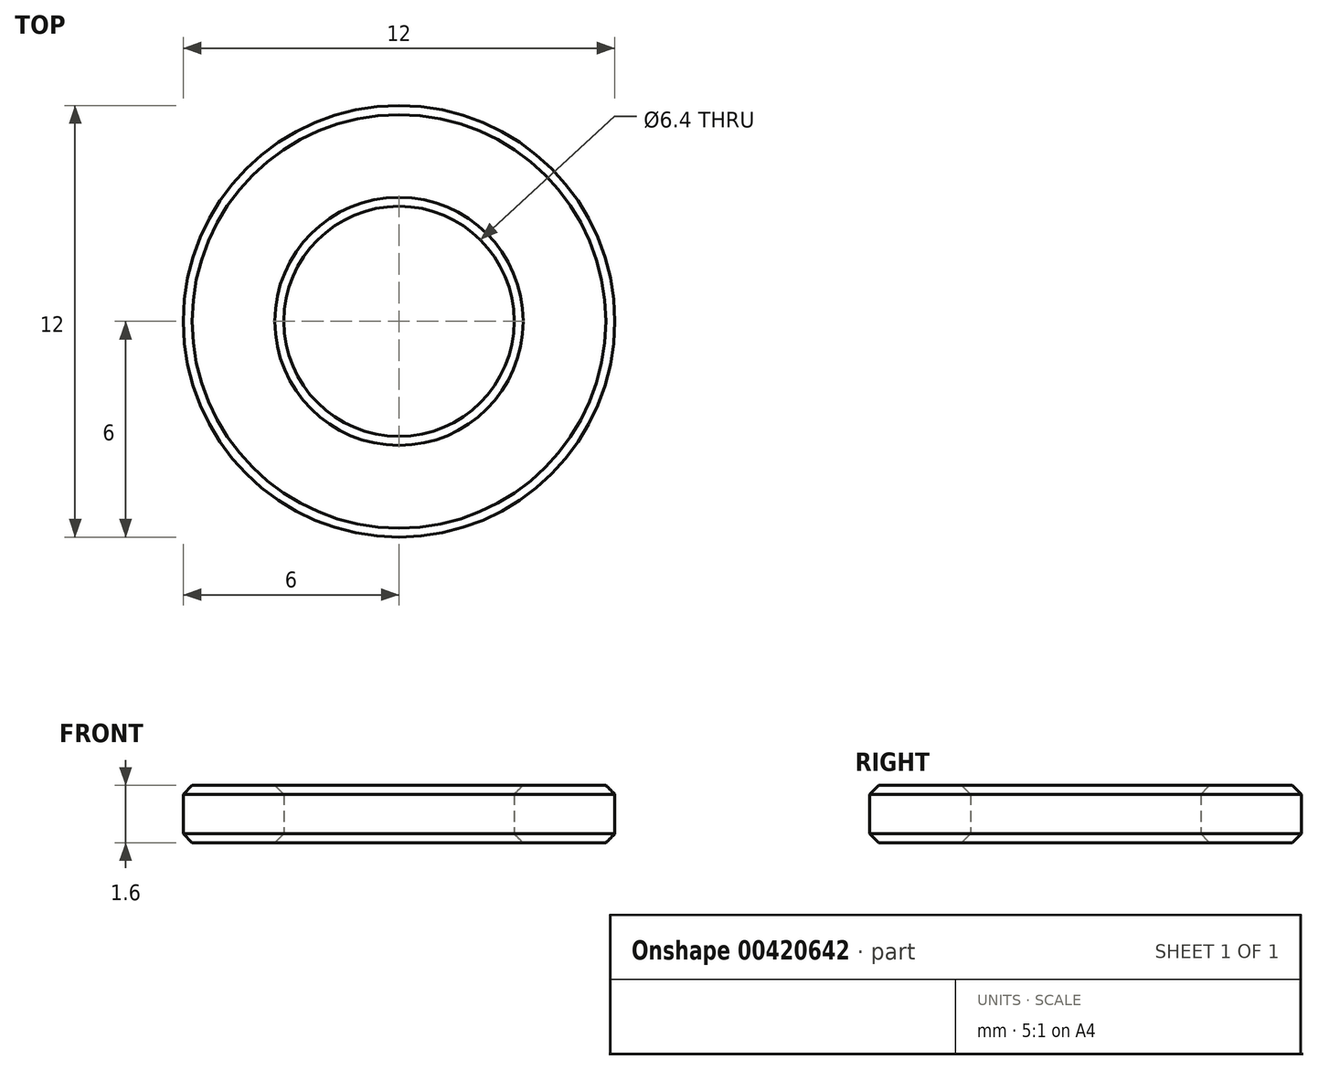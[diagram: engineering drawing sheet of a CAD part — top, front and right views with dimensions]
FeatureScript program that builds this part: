
annotation { "Feature Type Name" : "Feature", "Feature Type Description" : "" }
export const myFeature = defineFeature(function(context is Context, id is Id, definition is map)
    precondition{}
    {
        {
            var Q0;
            Q0=qCreatedBy(makeId("Top.planeOp"),FACE);
            var sketch = newSketch(context, id + "F0", { "sketchPlane" : qUnion([Q0])});
            skCircle(sketch, "E0", {"center": v(0, 0) * mm, "radius": 6 * mm});
            skCircle(sketch, "E1", {"center": v(0, 0) * mm, "radius": 3.2 * mm});
            skSolve(sketch);
        }
        {
            var Q0;
            Q0=makeQuery(id+"F0.imprint","IMPRINT",FACE,{"disambiguationData":[TD([[makeQuery(id+"F0.imprint","IMPRINT",EDGE,{"derivedFrom":sQuery(id+"F0.wireOp",EDGE,"E0")}),1.0]])]});
            extrude(context, id + "F1", {"entities" : qUnion([Q0]), "depth" : 1.6 * mm, "symmetric" : true});
        }
        {
            var Q0;
            Q0=makeQuery(id+"F1.opExtrude","CAP_EDGE",EDGE,{"disambiguationData":[OSD([sQuery(id+"F0.wireOp",EDGE,"E0")])],"isStart":false});
            var Q1;
            Q1=makeQuery(id+"F1.opExtrude","CAP_EDGE",EDGE,{"disambiguationData":[OSD([sQuery(id+"F0.wireOp",EDGE,"E0")])],"isStart":true});
            var Q2;
            Q2=makeQuery(id+"F1.opExtrude","CAP_EDGE",EDGE,{"disambiguationData":[OSD([sQuery(id+"F0.wireOp",EDGE,"E1")])],"isStart":false});
            var Q3;
            Q3=makeQuery(id+"F1.opExtrude","CAP_EDGE",EDGE,{"disambiguationData":[OSD([sQuery(id+"F0.wireOp",EDGE,"E1")])],"isStart":true});
            chamfer(context, id + "F2", {"entities" : qUnion([Q0, Q1, Q2, Q3]), "width" : 0.25 * mm, "tangentPropagation" : true});
        }
    });
